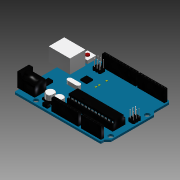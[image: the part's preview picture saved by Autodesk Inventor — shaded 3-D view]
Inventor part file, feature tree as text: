
AUTODESK INVENTOR PART (.ipt)
format: ipt  version: 2014 (Build 180170000, 170)  size: 1,532,416 bytes
history: native  units: in
note: dims shown in document units (in); Inventor stores cm internally (conversion verified against a paired STEP export)
features: sketch x39, extrude x38, fillet x15, chamfer x10, pattern_linear x8, projected_geometry x7, plane x1, mirror x1
ambient origin geometry x8: Origin, YZ Plane, XZ Plane, XY Plane, X Axis, Y Axis, Z Axis, Center Point
bodies: Solid1 (feature_tree), Body (feature_tree)
feature tree (119):
  fillet  "Board Fillets"  Radius=2.1in
  extrude  "Mount Holes"  Depth=2.6in
  extrude  "USB Body"  TaperAngle=135.0deg  [1 undecoded]
  extrude  "USB Hole"  Depth=1.3in
  extrude  "USB Center Pin"  Depth=0.06in TaperAngle=0.0deg
  extrude  "Power Plug Body 1"  Depth=0.14in
  extrude  "Power Plug Body 2"  Depth=0.05in
  extrude  "Power Plug Hole"  Depth=0.2in
  extrude  "Power Plug Pin"  Depth=0.6in
  fillet  "Power Plug Pin Rounded"  Radius=0.06in
  extrude  "Power Plug Bottom"  Depth=0.6385in
  fillet  "Power Plug Bottom Round"  Radius=0.25in
  fillet  "Power Plug Bottom Smooth"  Radius=0.35in
  fillet  "Power Plug Bottom Solder"  Radius=0.42in
  extrude  "USB Bottom"  Depth=0.05in
  fillet  "USB Bottom Round"  Radius=0.05in
  fillet  "USB Bottom Smooth"  Radius=0.05in
  fillet  "USB Bottom Solder"  [1 undecoded]
  extrude  "Pin Headers"  Depth=0.22in
  extrude  "Power Pin Group"  Depth=0.22in
  chamfer  "Power Pin Group Chamfer"  Distance=0.33in
  extrude  "Power Pin Group Bottom"  Depth=0.52in
  chamfer  "Power Pin Group Point"  Distance=0.43in
  fillet  "Power Pin Group Solder"  Radius=0.02in
  pattern_linear  "Rectangular Pattern3"  Spacing1=0.33in  [1 undecoded]
  extrude  "Analog Pin Group"  Depth=0.01in TaperAngle=45.0deg
  chamfer  "Analog Pin Group Chamfer"  Distance=0.02in
  extrude  "Analog Pin Group Bottom"  Depth=0.015in
  chamfer  "Analog Pin Group Point"  Distance=0.015in
  fillet  "Analog Pin Group Solder"  Radius=0.05in
  pattern_linear  "Rectangular Pattern4"  Spacing1=0.01in  [1 undecoded]
  extrude  "Data Pin Group 1"  Depth=0.03in
  chamfer  "Data Pin Group 1 Chamfer"  Distance=0.1in
  extrude  "Data Pin Group 1 Bottom"  Depth=0.05in
  chamfer  "Data Pin Group 1 Point"  Distance=0.02in
  fillet  "Data Pin Group 1 Solder"  Radius=0.03in
  pattern_linear  "Rectangular Pattern5"  Spacing1=0.03in  [1 undecoded]
  extrude  "Data Pin Group 2"  Depth=0.03in
  chamfer  "Data Pin Group 2 Chamfer"  Distance=0.03in
  extrude  "Data Pin Group 2 Bottom"  Depth=0.03in
  chamfer  "Data Pin Group 2 Point"  Distance=0.03in
  fillet  "Data Pin Group 2 Solder"  Radius=0.33in
  pattern_linear  "Rectangular Pattern6"  Spacing1=0.01in  [1 undecoded]
  extrude  "Microprocessor Socket"  Depth=0.02in
  extrude  "Microprocessor"  Depth=0.05in TaperAngle=0.0deg
  extrude  "Microprocessor Pins"  Depth=0.01in TaperAngle=45.0deg
  pattern_linear  "Rectangular Pattern7"  Spacing1=0.03in  [1 undecoded]
  extrude  "Microprocessor End Pins"  Depth=0.1in
  plane  "Work Plane1"
  mirror  "Mirror1"
  extrude  "ICSP Pin Base"  Depth=0.03in
  extrude  "ICSP Pin"  Depth=0.03in
  pattern_linear  "Rectangular Pattern8"  Spacing1=0.03in  [1 undecoded]
  extrude  "AREF Pin Base"  Depth=0.03in
  extrude  "AREF Pin"  Depth=0.33in TaperAngle=0.0deg
  pattern_linear  "Rectangular Pattern9"  Spacing1=0.01in  [1 undecoded]
  extrude  "Reset Button Base"  Depth=0.02in
  extrude  "Reset Button"  Depth=0.05in TaperAngle=0.0deg
  extrude  "Extrusion31"  Depth=0.01in TaperAngle=45.0deg
  extrude  "Extrusion32"  Depth=0.03in
  fillet  "Fillet13"  Radius=0.1in
  extrude  "Extrusion33"  Depth=0.03in
  extrude  "Extrusion34"  Depth=0.03in
  extrude  "Extrusion35"  Depth=0.03in
  extrude  "Extrusion36"  Depth=0.03in
  extrude  "Extrusion37"  Depth=0.33in TaperAngle=0.0deg
  extrude  "Extrusion38"  Depth=0.02in
  chamfer  "Chamfer9"  Distance=0.05in
  fillet  "Fillet14"  Radius=0.01in
  extrude  "Extrusion39"  Depth=0.03in
  chamfer  "Chamfer10"  Distance=0.01in Angle=45.0deg
  fillet  "Fillet15"  Radius=0.1in
  pattern_linear  "Rectangular Pattern10"  Spacing1=0.1in  [1 undecoded]
  sketch  "Sketch1"  dims[d2=2.7in d3=2.6in]
  sketch  "Sketch2"  dims[d4=0.05in d5=135.0deg]
  sketch  "Sketch3"  dims[d6=0.6in d7=1.3in]
  sketch  "Sketch4"  dims[d8=135.0deg d9=0.06in d10=0.0in]
  sketch  "Sketch5"  dims[d11=0.025in d12=0.14in]
  sketch  "Sketch6"  dims[d13=2.0in d14=0.05in]
  sketch  "Sketch7"  dims[d15=0.1in d16=0.2in]
  sketch  "Sketch8"  dims[d17=1.1in d18=0.6in d19=0.06in d20=0.0in]
  sketch  "Sketch9"  dims[d21=0.4665in d22=0.6385in d23=0.25in d24=0.35in d25=0.42in d26=0.0in]
  sketch  "Sketch10"  dims[d27=0.05in d28=0.05in d29=0.05in d30=0.05in d31=135.0deg]
  sketch  "Sketch11"  dims[d32=135.0deg d33=0.22in]
  sketch  "Sketch12"  dims[d34=0.35in d35=0.0in d36=0.22in]
  projected_geometry  "Projected Loop1"
  sketch  "Sketch13"  dims[d37=0.12in]
  projected_geometry  "Projected Loop2"
  sketch  "Sketch14"  dims[d38=0.1in d39=0.33in d40=0.0in]
  projected_geometry  "Projected Loop3"
  sketch  "Sketch15"  dims[d41=0.35in d42=0.52in]
  sketch  "Sketch16"  dims[d43=0.15in]
  projected_geometry  "Projected Loop4"
  sketch  "Sketch17"  dims[d44=0.06in d45=0.43in d46=0.0in d47=0.02in]
  sketch  "Sketch18"  dims[d48=0.4in d49=0.0in]
  projected_geometry  "Projected Loop5"
  sketch  "Sketch19"  dims[d50=0.25in]
  sketch  "Sketch20"  dims[d51=0.0425in]
  sketch  "Sketch21"  dims[d52=0.39in d53=0.0in]
  sketch  "Sketch22"  dims[d54=0.05in]
  sketch  "Sketch23"  dims[d55=0.32in d56=0.0in]
  sketch  "Sketch24"  dims[d57=0.025in]
  sketch  "Sketch25"  dims[d58=0.09in]
  sketch  "Sketch26"  dims[d59=0.81in]
  sketch  "Sketch27"  dims[d60=0.085in]
  sketch  "Sketch28"  dims[d61=0.6in]
  sketch  "Sketch29"  dims[d62=0.6in]
  sketch  "Sketch30"  dims[d63=0.05in]
  sketch  "Sketch31"  dims[d64=0.82in]
  sketch  "Sketch32"  dims[d65=0.05in]
  projected_geometry  "Projected Loop6"
  sketch  "Sketch33"  dims[d66=1.01in]
  sketch  "Sketch34"  dims[d67=0.05in]
  sketch  "Sketch35"  dims[d68=0.35in d69=0.0in]
  sketch  "Sketch36"  dims[d70=0.03in]
  sketch  "Sketch37"  dims[d71=0.03in]
  sketch  "Sketch38"  dims[d72=0.03in]
  sketch  "Sketch39"  dims[d73=0.03in d74=0.33in d75=0.0in d76=0.01in d77=0.125in d78=45.0deg d85=0.02in d86=0.015in d87=0.015in d88=0.05in d89=0.0in d90=0.01in d91=0.125in d92=45.0deg d93=0.03in d94=3.1496in d96=0.1in d97=0.05in d98=0.02in d99=0.03in d100=0.03in d101=0.03in d102=0.03in d103=0.03in d104=0.03in d105=0.33in d106=0.0in d107=0.01in d108=0.125in d109=45.0deg d110=0.02in d111=0.05in d112=0.0in d113=0.01in d114=0.125in d115=45.0deg d116=0.03in d117=2.3622in d119=0.1in d120=0.03in d121=0.03in d122=0.03in d123=0.03in d124=0.33in d125=0.0in d126=0.01in d127=0.125in d128=45.0deg d129=0.02in d130=0.05in d131=0.0in d132=0.01in d133=0.125in d134=45.0deg d135=0.03in d136=3.1496in d138=0.1in d139=0.03in d140=0.03in d141=0.03in d142=0.03in d143=0.33in d144=0.0in d145=0.02in d146=0.05in d147=0.0in d148=0.01in d149=0.125in d150=45.0deg d151=0.03in d152=0.01in d153=0.125in d154=45.0deg d155=3.937in d157=0.1in d158=0.1in d159=0.02in d160=0.25in d161=0.28in d162=0.23in d163=0.36in d164=0.11in d165=0.1in d166=0.0in d167=0.05in d168=0.005in d169=0.05in d170=0.01in d171=0.06in d172=0.48in d173=0.0067in d174=0.0067in d175=0.135in d176=0.1in d177=0.0in d178=0.025in d179=0.005in d180=0.025in d181=0.38in d182=1.38in d183=0.3in d184=0.18in d185=0.18in d186=0.0in d187=0.275in d188=0.0525in d189=0.0525in d190=0.1in d191=0.0in d192=0.065in d193=0.04in d194=0.124in d195=0.01in d196=0.0in d197=4.7244in d199=0.1in d200=0.0325in d202=0.0325in d203=0.01in d204=0.0in d205=-0.1875in d206=0.04in d207=0.185in d208=0.05in d209=0.12in d210=0.08in d211=0.0in d212=0.02in d213=0.23in d214=0.0in d215=1.1811in d217=0.08in d218=0.04in d219=0.185in d220=0.04in d221=0.185in d223=0.13in d224=0.08in d225=0.0in d226=0.02in d227=0.23in d228=0.0in d229=1.1811in d231=0.08in d232=0.26in d233=0.26in d234=0.02in d235=0.12in d236=0.1in d237=0.0in d238=0.11in d239=0.03in d240=0.0in d241=0.25in d242=0.02in d243=0.21in d244=0.05in d245=0.0in d246=0.16in d247=0.0in d248=0.025in d249=0.15in d250=0.1in d251=0.05in d252=0.12in d253=0.09in d254=0.0in d255=0.065in d256=0.38in d257=0.55in d258=0.62in d259=0.11in d260=0.0in d261=0.19in d262=0.19in d263=0.17in d264=0.31in d265=0.04in d266=0.0in d267=0.05in d268=0.04in d269=0.2675in d270=0.173in d271=0.05in d272=0.2in d273=0.01in d274=0.0in d275=0.13in d276=0.21in d277=0.465in d278=0.21in d279=0.065in d280=0.0in d281=0.05in d282=0.0in d283=0.01in d284=0.125in d285=45.0deg d286=0.02in d288=0.37in d289=0.05in d290=0.0in d291=0.01in d292=0.125in d293=45.0deg d294=0.03in d295=5.5118in d297=0.1025in d298=0.7874in d300=0.25in]
  projected_geometry  "Projected Loop7"
note: 10 required parameter values undecoded (feature->parameter linkage not recoverable at this tier; creation-order binding heuristic only, values carry confidence <= 0.55)
